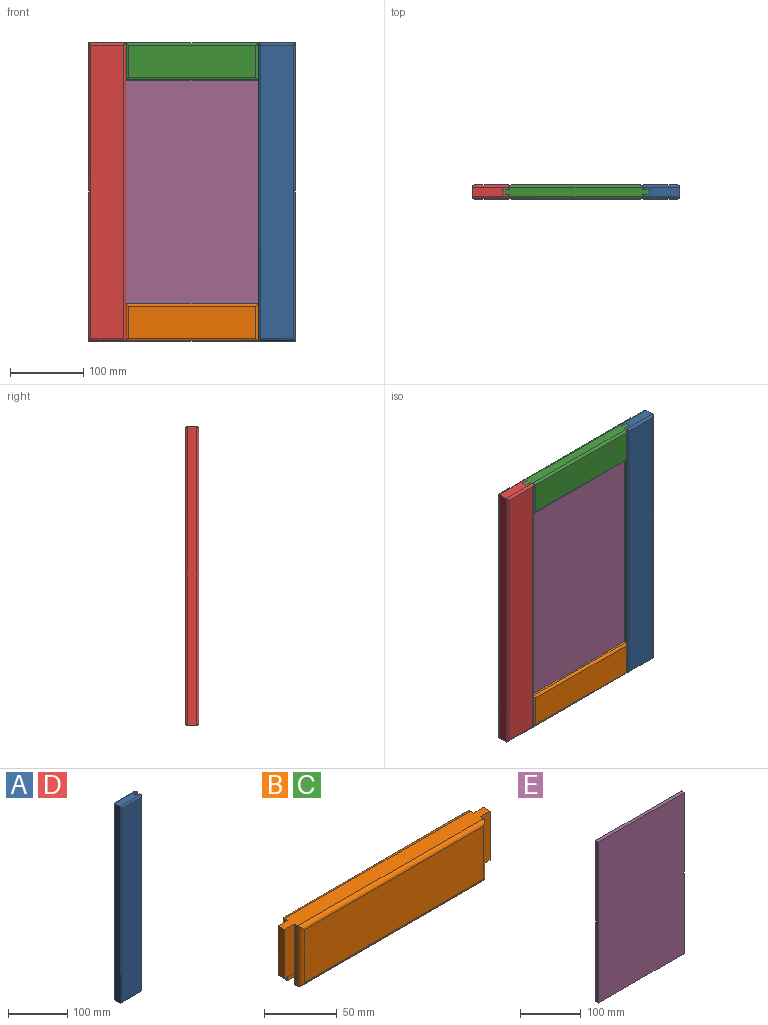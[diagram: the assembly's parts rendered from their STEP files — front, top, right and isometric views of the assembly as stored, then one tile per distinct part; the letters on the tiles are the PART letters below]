
ASSEMBLY  parts=5 mates=12
PART A: 18 faces, bbox 50.8x19.1x406.4 mm
  f0: plane 406.4x3.18mm, normal (1,0,0), area 1290.3mm2, adj f1,f4,f7,f14
  f1: plane 50.8x12.7mm, normal (0,0,1), area 584.7mm2, adj f0,f2,f3,f7,f8,f9,f11,f15
  f2: plane 406.4x3.18mm, normal (1,0,0), area 1290.3mm2, adj f1,f4,f9,f10
  f3: plane 406.4x12.7mm, normal (-1,0,0), area 5161.3mm2, adj f1,f4,f13,f17
  f4: plane 50.8x12.7mm, normal (0,0,-1), area 584.7mm2, adj f0,f2,f3,f7,f8,f9,f12,f16
  f5: plane 400.05x44.45mm, normal (0,1,0), area 17782.2mm2, adj f14,f15,f16,f17
  f6: plane 400.05x44.45mm, normal (0,-1,0), area 17782.2mm2, adj f10,f11,f12,f13
  f7: plane 406.4x9.53mm, normal (0,-1,0), area 3871mm2, adj f0,f1,f4,f8
  f8: plane 406.4x6.35mm, normal (1,0,0), area 2580.6mm2, adj f1,f4,f7,f9
  f9: plane 406.4x9.53mm, normal (0,1,0), area 3871mm2, adj f1,f2,f4,f8
  f10: cylinder r=3.17mm len=406.4mm, axis (0,0,1), area 2015.3mm2, adj f2,f6,f11,f12
  f11: cylinder r=3.17mm len=50.8mm, axis (-1,0,0), area 241.8mm2, adj f1,f6,f10,f13
  f12: cylinder r=3.17mm len=50.8mm, axis (1,0,0), area 241.8mm2, adj f4,f6,f10,f13
  f13: cylinder r=3.17mm len=406.4mm, axis (0,0,-1), area 2015.3mm2, adj f3,f6,f11,f12
  f14: cylinder r=3.17mm len=406.4mm, axis (0,0,-1), area 2015.3mm2, adj f0,f5,f15,f16
  f15: cylinder r=3.17mm len=50.8mm, axis (1,0,0), area 241.8mm2, adj f1,f5,f14,f17
  f16: cylinder r=3.17mm len=50.8mm, axis (-1,0,0), area 241.8mm2, adj f4,f5,f14,f17
  f17: cylinder r=3.17mm len=406.4mm, axis (0,0,1), area 2015.3mm2, adj f3,f5,f15,f16
PART B: 26 faces, bbox 199.6x19.1x50.8 mm
  f0: plane 50.8x3.18mm, normal (-1,0,0), area 161.3mm2, adj f4,f5,f10,f16,f23
  f1: plane 50.8x3.18mm, normal (1,0,0), area 161.3mm2, adj f4,f5,f10,f12,f24
  f2: plane 180.58x3.18mm, normal (0,0,-1), area 573.3mm2, adj f3,f6,f9,f21
  f3: plane 50.8x3.18mm, normal (-1,0,0), area 161.3mm2, adj f2,f4,f9,f15,f19
  f4: plane 199.63x12.7mm, normal (0,0,1), area 2414.3mm2, adj f0,f1,f3,f6,f12,f13,f14,f15
  f5: plane 180.58x3.18mm, normal (0,0,-1), area 573.3mm2, adj f0,f1,f10,f25
  f6: plane 50.8x3.18mm, normal (1,0,0), area 161.3mm2, adj f2,f4,f9,f13,f20
  f7: plane 174.23x44.45mm, normal (0,1,0), area 7744.4mm2, adj f22,f23,f24,f25
  f8: plane 174.23x44.45mm, normal (0,-1,0), area 7744.4mm2, adj f18,f19,f20,f21
  f9: plane 180.58x9.53mm, normal (0,1,0), area 1720mm2, adj f2,f3,f6,f11
  f10: plane 180.58x9.53mm, normal (0,-1,0), area 1720mm2, adj f0,f1,f5,f11
  f11: plane 199.63x6.35mm, normal (0,0,-1), area 1267.6mm2, adj f9,f10,f12,f13,f14,f15,f16,f17
  f12: plane 41.28x9.53mm, normal (0,1,0), area 393.1mm2, adj f1,f4,f11,f14
  f13: plane 41.28x9.53mm, normal (0,-1,0), area 393.1mm2, adj f4,f6,f11,f14
  f14: plane 41.28x6.35mm, normal (1,0,0), area 262.1mm2, adj f4,f11,f12,f13
  f15: plane 41.28x9.53mm, normal (0,-1,0), area 393.1mm2, adj f3,f4,f11,f17
  f16: plane 41.28x9.53mm, normal (0,1,0), area 393.1mm2, adj f0,f4,f11,f17
  f17: plane 41.28x6.35mm, normal (-1,0,0), area 262.1mm2, adj f4,f11,f15,f16
  f18: cylinder r=3.17mm len=180.58mm, axis (-1,0,0), area 889.1mm2, adj f4,f8,f19,f20
  f19: cylinder r=3.17mm len=50.8mm, axis (0,0,-1), area 241.8mm2, adj f3,f8,f18,f21
  f20: cylinder r=3.17mm len=50.8mm, axis (0,0,1), area 241.8mm2, adj f6,f8,f18,f21
  f21: cylinder r=3.17mm len=180.58mm, axis (1,0,0), area 889.1mm2, adj f2,f8,f19,f20
  f22: cylinder r=3.17mm len=180.58mm, axis (1,0,0), area 889.1mm2, adj f4,f7,f23,f24
  f23: cylinder r=3.17mm len=50.8mm, axis (0,0,1), area 241.8mm2, adj f0,f7,f22,f25
  f24: cylinder r=3.17mm len=50.8mm, axis (0,0,-1), area 241.8mm2, adj f1,f7,f22,f25
  f25: cylinder r=3.17mm len=180.58mm, axis (-1,0,0), area 889.1mm2, adj f5,f7,f23,f24
PART C: same geometry as B
PART D: same geometry as A
PART E: 6 faces, bbox 199.6x6.4x323.9 mm
  f0: plane 323.85x6.35mm, normal (1,0,0), area 2056.4mm2, adj f1,f3,f4,f5
  f1: plane 323.85x199.63mm, normal (0,1,0), area 64649.6mm2, adj f0,f2,f3,f4
  f2: plane 323.85x6.35mm, normal (-1,0,0), area 2056.4mm2, adj f1,f3,f4,f5
  f3: plane 199.63x6.35mm, normal (0,0,1), area 1267.6mm2, adj f0,f1,f2,f5
  f4: plane 199.63x6.35mm, normal (0,0,-1), area 1267.6mm2, adj f0,f1,f2,f5
  f5: plane 323.85x199.63mm, normal (0,-1,0), area 64649.6mm2, adj f0,f2,f3,f4
PLACE A rot(axis=(0,0,1),180deg) t=(-1.29,-247.69,-294.31)mm
PLACE B rot(axis=(1,0,0),180deg) t=(283.27,-247.69,-111.74)mm
PLACE C t=(283.27,266.66,-294.31)mm
PLACE D t=(283.27,266.66,-294.31)mm fixed
PLACE E at identity
MATE planar A.f9 <-> E.f1  axis (0,-1,0) through (236.05,12.66,-203.03)mm
MATE planar B.f4 <-> D.f4  axis (0,0,-1) through (140.99,9.48,-406.23)mm
MATE planar B.f17 <-> D.f8  axis (-1,0,0) through (41.18,9.48,-385.59)mm
MATE planar B.f4 <-> A.f4  axis (0,0,-1) through (140.99,9.48,-406.23)mm
MATE planar B.f7 <-> D.f6  axis (0,-1,0) through (140.99,-0.04,-380.83)mm
MATE planar B.f11 <-> E.f4  axis (0,0,1) through (140.99,9.48,-364.95)mm
MATE planar B.f14 <-> A.f8  axis (1,0,0) through (240.81,9.48,-385.59)mm
MATE planar A.f5 <-> B.f7  axis (0,-1,0) through (256.68,-0.04,-203.03)mm
MATE planar D.f8 <-> E.f2  axis (1,0,0) through (41.18,9.48,-203.03)mm
MATE planar C.f4 <-> A.f1  axis (0,0,1) through (140.99,9.48,0.17)mm
MATE planar D.f6 <-> C.f8  axis (0,-1,0) through (25.3,-0.04,-203.03)mm
MATE planar A.f8 <-> C.f14  axis (-1,0,0) through (240.81,9.48,0.17)mm
